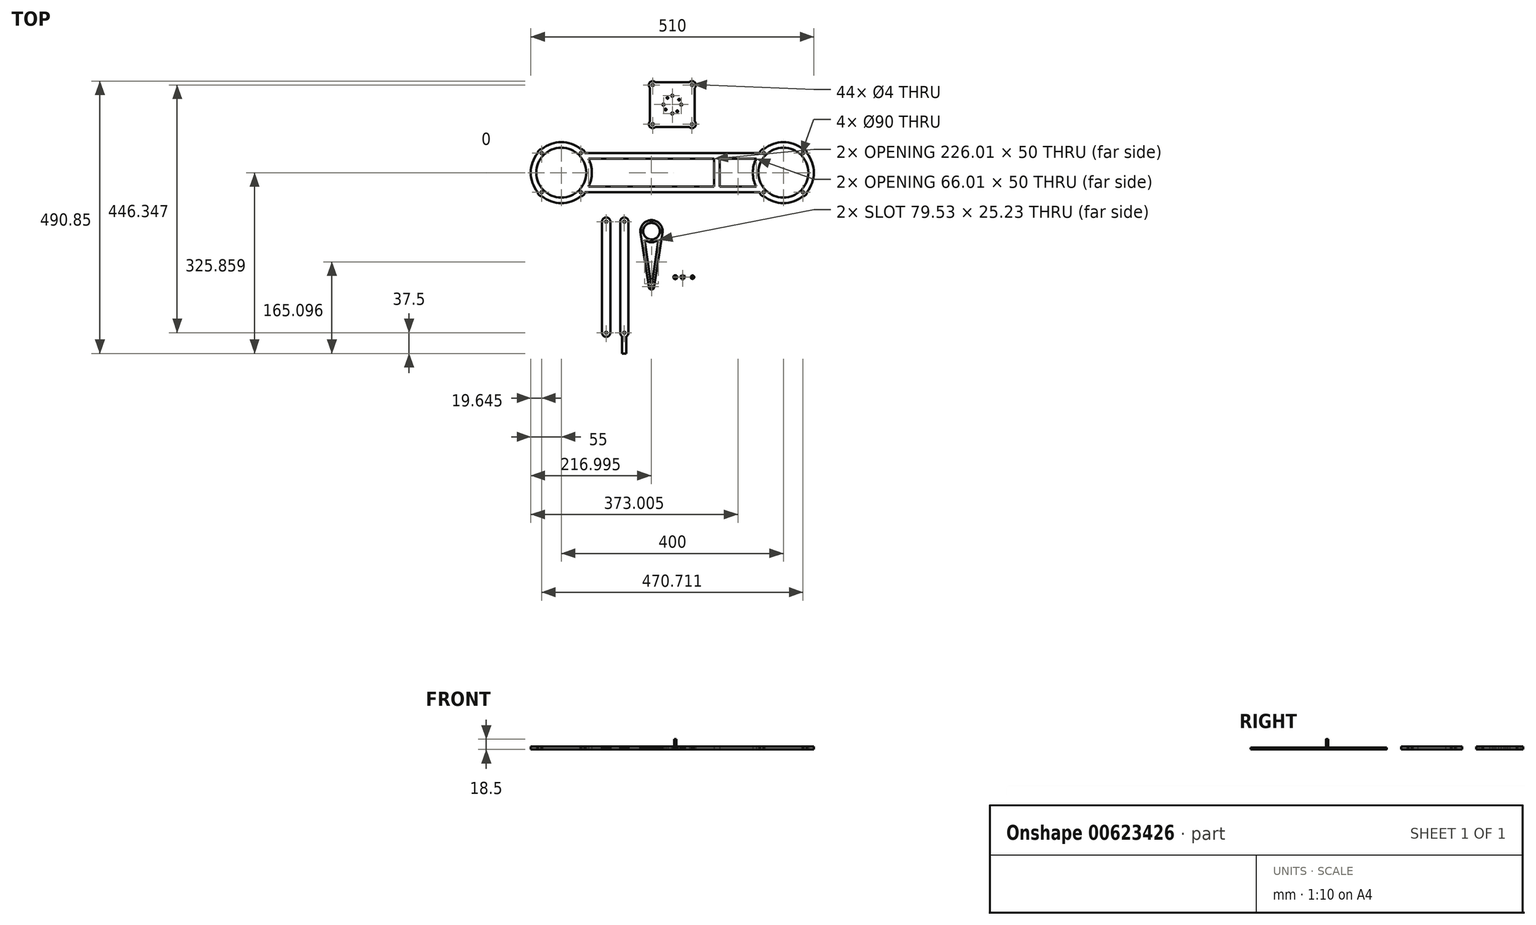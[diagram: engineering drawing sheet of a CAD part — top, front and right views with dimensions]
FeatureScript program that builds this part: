
annotation { "Feature Type Name" : "Feature", "Feature Type Description" : "" }
export const myFeature = defineFeature(function(context is Context, id is Id, definition is map)
    precondition{}
    {
        {
            assignVariable(context, id + "F0", {"name" : "AluThickness", "anyValue" : 3});
        }
        {
            var Q0;
            Q0=qCreatedBy(makeId("Top.planeOp"),FACE);
            var sketch = newSketch(context, id + "F1", { "sketchPlane" : qUnion([Q0])});
            skLineSegment(sketch, "E0.bottom", {"start": v(-111.65, 100) * mm, "end": v(-126.65, 100) * mm});
            skLineSegment(sketch, "E0.top", {"start": v(-111.65, -100) * mm, "end": v(-126.65, -100) * mm});
            skLineSegment(sketch, "E0.left", {"start": v(-111.65, 100) * mm, "end": v(-111.65, -100) * mm});
            skLineSegment(sketch, "E0.right", {"start": v(-126.65, 100) * mm, "end": v(-126.65, -100) * mm});
            skPoint(sketch, "E0.middle", {"position": v(-119.15, 0) * mm});
            skCircle(sketch, "E1", {"center": v(-119.15, 100) * mm, "radius": 7.5 * mm});
            skCircle(sketch, "E2", {"center": v(-119.15, -100) * mm, "radius": 7.5 * mm});
            skLineSegment(sketch, "E3.bottom", {"start": v(-79.02, 100) * mm, "end": v(-94.02, 100) * mm});
            skLineSegment(sketch, "E3.top", {"start": v(-79.02, -100) * mm, "end": v(-94.02, -100) * mm});
            skLineSegment(sketch, "E3.left", {"start": v(-79.02, 100) * mm, "end": v(-79.02, -100) * mm});
            skLineSegment(sketch, "E3.right", {"start": v(-94.02, 100) * mm, "end": v(-94.02, -100) * mm});
            skPoint(sketch, "E3.middle", {"position": v(-86.52, 0) * mm});
            skCircle(sketch, "E4", {"center": v(-86.52, 100) * mm, "radius": 7.5 * mm});
            skCircle(sketch, "E5", {"center": v(-86.52, -100) * mm, "radius": 7.5 * mm});
            skCircle(sketch, "E6", {"center": v(-119.15, 100) * mm, "radius": 2 * mm});
            skCircle(sketch, "E7", {"center": v(-119.15, -100) * mm, "radius": 2 * mm});
            skCircle(sketch, "E8", {"center": v(-86.52, 100) * mm, "radius": 2 * mm});
            skCircle(sketch, "E9", {"center": v(-86.52, -100) * mm, "radius": 2 * mm});
            skLineSegment(sketch, "E10.bottom", {"start": v(-82.93, -137.5) * mm, "end": v(-90.43, -137.5) * mm});
            skLineSegment(sketch, "E10.left", {"start": v(-82.93, -137.5) * mm, "end": v(-82.93, -106.59) * mm});
            skLineSegment(sketch, "E10.right", {"start": v(-90.43, -137.5) * mm, "end": v(-90.43, -106.4) * mm});
            skPoint(sketch, "E10.middle", {"position": v(-86.68, -107.5) * mm});
            skPoint(sketch, "E10.top.end.orphan", {"position": v(-90.43, -77.5) * mm});
            skPoint(sketch, "E11.orphan", {"position": v(-82.93, -77.5) * mm});
            skCircle(sketch, "E12", {"center": v(-37.56, 82.88) * mm, "radius": 20 * mm});
            skCircle(sketch, "E13", {"center": v(-37.56, -17.12) * mm, "radius": 2 * mm});
            skCircle(sketch, "E14.0", {"center": v(-37.56, -17.12) * mm, "radius": 5 * mm});
            skLineSegment(sketch, "E15", {"start": v(-57.56, 82.88) * mm, "end": v(-42.56, -17.12) * mm});
            skLineSegment(sketch, "E16", {"start": v(-32.56, -17.12) * mm, "end": v(-17.56, 82.88) * mm});
            skCircle(sketch, "E17", {"center": v(-37.56, 82.88) * mm, "radius": 15 * mm});
            skCircle(sketch, "E18", {"center": v(-37.56, 82.88) * mm, "radius": 17.5 * mm, "construction": true});
            skCircle(sketch, "E19", {"center": v(-37.56, 100.38) * mm, "radius": 1.5 * mm});
            skCircle(sketch, "E20.1.0", {"center": v(-55.06, 82.88) * mm, "radius": 1.5 * mm});
            skCircle(sketch, "E20.2.0", {"center": v(-37.56, 65.38) * mm, "radius": 1.5 * mm});
            skCircle(sketch, "E20.3.0", {"center": v(-20.06, 82.88) * mm, "radius": 1.5 * mm});
            skLineSegment(sketch, "E21.0", {"start": v(-52.61, 83.62) * mm, "end": v(-52.55, 83.22) * mm});
            skLineSegment(sketch, "E22.trimOffspring", {"start": v(-50.18, 67.36) * mm, "end": v(-38.25, -12.17) * mm});
            skLineSegment(sketch, "E23.trimOffspring", {"start": v(-22.56, 83.22) * mm, "end": v(-22.5, 83.62) * mm});
            skLineSegment(sketch, "E24.trimOffspring", {"start": v(-36.87, -12.17) * mm, "end": v(-24.94, 67.36) * mm});
            skSolve(sketch);
        }
        {
            var Q0;
            Q0 = qSketchRegion(id + "F1", true);
            extrude(context, id + "F2", {"entities" : qUnion([Q0]), "depth" : (getVariable(context, 'AluThickness')) * mm, "offsetDistance" : 25 * mm});
        }
        {
            var Q0;
            Q0=qCreatedBy(makeId("Top.planeOp"),FACE);
            var sketch = newSketch(context, id + "F3", { "sketchPlane" : qUnion([Q0])});
            skCircle(sketch, "E25", {"center": v(5.28, 0) * mm, "radius": 3.5 * mm});
            skCircle(sketch, "E26.cCircle", {"center": v(18.64, 0) * mm, "radius": 3.5 * mm, "construction": true});
            skLineSegment(sketch, "E26.0", {"start": v(20.66, -3.5) * mm, "end": v(16.62, -3.5) * mm});
            skLineSegment(sketch, "E26.1", {"start": v(16.62, -3.5) * mm, "end": v(14.6, 0) * mm});
            skLineSegment(sketch, "E26.2", {"start": v(14.6, 0) * mm, "end": v(16.62, 3.5) * mm});
            skLineSegment(sketch, "E26.3", {"start": v(16.62, 3.5) * mm, "end": v(20.66, 3.5) * mm});
            skLineSegment(sketch, "E26.4", {"start": v(20.66, 3.5) * mm, "end": v(22.68, 0) * mm});
            skLineSegment(sketch, "E26.5", {"start": v(22.68, 0) * mm, "end": v(20.66, -3.5) * mm});
            skPoint(sketch, "E26.0.midPoint", {"position": v(18.64, -3.5) * mm});
            skCircle(sketch, "E27", {"center": v(18.64, 0) * mm, "radius": 2 * mm});
            skCircle(sketch, "E28", {"center": v(36.28, 0) * mm, "radius": 3 * mm});
            skCircle(sketch, "E29", {"center": v(36.28, 0) * mm, "radius": 2 * mm});
            skSolve(sketch);
        }
        {
            var Q0;
            Q0=makeQuery(id+"F3.imprint","IMPRINT",FACE,{"disambiguationData":[TD([[makeQuery(id+"F3.imprint","IMPRINT",EDGE,{"derivedFrom":sQuery(id+"F3.wireOp",EDGE,"E25")}),1.0]])]});
            var Q1;
            Q1=makeQuery(id+"F3.imprint","IMPRINT",FACE,{"disambiguationData":[TD([[makeQuery(id+"F3.imprint","IMPRINT",EDGE,{"derivedFrom":sQuery(id+"F3.wireOp",EDGE,"E26.0")}),-1.0]])]});
            extrude(context, id + "F4", {"entities" : qUnion([Q0, Q1]), "depth" : 3 * mm, "offsetDistance" : 25 * mm});
        }
        {
            var Q0;
            Q0=makeQuery(id+"F3.imprint","IMPRINT",FACE,{"disambiguationData":[TD([[makeQuery(id+"F3.imprint","IMPRINT",EDGE,{"derivedFrom":sQuery(id+"F3.wireOp",EDGE,"E28")}),1.0]])]});
            extrude(context, id + "F5", {"entities" : qUnion([Q0]), "depth" : 1 * mm, "offsetDistance" : 25 * mm});
        }
        {
            var Q0;
            Q0=makeQuery(id+"F5.opExtrude","CAP_FACE",FACE,{"disambiguationData":[OSD([sQuery(id+"F3.wireOp",EDGE,"E28"),sQuery(id+"F3.wireOp",EDGE,"E29")])],"isStart":false});
            var sketch = newSketch(context, id + "F6", { "sketchPlane" : qUnion([Q0])});
            skCircle(sketch, "E30", {"center": v(36.28, 0) * mm, "radius": 3.1 * mm});
            skSolve(sketch);
        }
        {
            var Q0;
            Q0=makeQuery(id+"F3.imprint","IMPRINT",FACE,{"disambiguationData":[TD([[makeQuery(id+"F3.imprint","IMPRINT",EDGE,{"derivedFrom":sQuery(id+"F3.wireOp",EDGE,"E29")}),1.0]])]});
            var sketch = newSketch(context, id + "F7", { "sketchPlane" : qUnion([Q0])});
            skCircle(sketch, "E31", {"center": v(36.28, 0) * mm, "radius": 3.1 * mm});
            skSolve(sketch);
        }
        {
            var Q0;
            Q0=makeQuery(id+"F6.imprint","IMPRINT",FACE,{"disambiguationData":[TD([[makeQuery(id+"F6.imprint","IMPRINT",EDGE,{"derivedFrom":sQuery(id+"F6.wireOp",EDGE,"E30")}),1.0]])]});
            var Q1;
            Q1=makeQuery(id+"F6.imprint","IMPRINT",FACE,{"disambiguationData":[TD([[makeQuery(id+"F6.imprint","IMPRINT",EDGE,{"derivedFrom":makeQuery(id+"F5.opExtrude","CAP_EDGE",EDGE,{"disambiguationData":[OSD([sQuery(id+"F3.wireOp",EDGE,"E28")])],"isStart":false})}),1.0]])]});
            extrude(context, id + "F8", {"entities" : qUnion([Q0, Q1]), "operationType" : NewBodyOperationType.ADD, "depth" : .5 * mm, "offsetDistance" : 25 * mm});
        }
        {
            var Q0;
            Q0=makeQuery(id+"F7.imprint","IMPRINT",FACE,{"disambiguationData":[TD([[makeQuery(id+"F7.imprint","IMPRINT",EDGE,{"derivedFrom":sQuery(id+"F7.wireOp",EDGE,"E31")}),1.0]])]});
            extrude(context, id + "F9", {"entities" : qUnion([Q0]), "operationType" : NewBodyOperationType.ADD, "oppositeDirection" : true, "depth" : .5 * mm, "offsetDistance" : 25 * mm});
        }
        {
            var Q0;
            Q0=makeQuery(id+"F4.opExtrude","CAP_FACE",FACE,{"disambiguationData":[OSD([sQuery(id+"F3.wireOp",EDGE,"E25")])],"isStart":true});
            var sketch = newSketch(context, id + "F10", { "sketchPlane" : qUnion([Q0])});
            skCircle(sketch, "E32.cCircle", {"center": v(5.28, 0) * mm, "radius": 2 * mm, "construction": true});
            skLineSegment(sketch, "E32.0", {"start": v(6.44, -2) * mm, "end": v(4.13, -2) * mm});
            skLineSegment(sketch, "E32.1", {"start": v(4.13, -2) * mm, "end": v(2.97, 0) * mm});
            skLineSegment(sketch, "E32.2", {"start": v(2.97, 0) * mm, "end": v(4.13, 2) * mm});
            skLineSegment(sketch, "E32.3", {"start": v(4.13, 2) * mm, "end": v(6.44, 2) * mm});
            skLineSegment(sketch, "E32.4", {"start": v(6.44, 2) * mm, "end": v(7.59, 0) * mm});
            skLineSegment(sketch, "E32.5", {"start": v(7.59, 0) * mm, "end": v(6.44, -2) * mm});
            skPoint(sketch, "E32.0.midPoint", {"position": v(5.28, -2) * mm});
            skSolve(sketch);
        }
        {
            var Q0;
            Q0=makeQuery(id+"F10.imprint","IMPRINT",FACE,{"disambiguationData":[TD([[makeQuery(id+"F10.imprint","IMPRINT",EDGE,{"derivedFrom":sQuery(id+"F10.wireOp",EDGE,"E32.0")}),-1.0]])]});
            extrude(context, id + "F11", {"entities" : qUnion([Q0]), "operationType" : NewBodyOperationType.REMOVE, "oppositeDirection" : true, "depth" : 2 * mm, "offsetDistance" : 25 * mm});
        }
        {
            var Q0;
            Q0=makeQuery(id+"F4.opExtrude","CAP_FACE",FACE,{"disambiguationData":[OSD([sQuery(id+"F3.wireOp",EDGE,"E25")])],"isStart":false});
            var sketch = newSketch(context, id + "F12", { "sketchPlane" : qUnion([Q0])});
            skCircle(sketch, "E33", {"center": v(5.28, 0) * mm, "radius": 2 * mm});
            skSolve(sketch);
        }
        {
            var Q0;
            Q0=makeQuery(id+"F12.imprint","IMPRINT",FACE,{"disambiguationData":[TD([[makeQuery(id+"F12.imprint","IMPRINT",EDGE,{"derivedFrom":sQuery(id+"F12.wireOp",EDGE,"E33")}),1.0]])]});
            extrude(context, id + "F13", {"entities" : qUnion([Q0]), "operationType" : NewBodyOperationType.ADD, "depth" : (getVariable(context, 'AluThickness') * 5) * mm, "offsetDistance" : 25 * mm});
        }
        {
            var Q0;
            Q0=qCreatedBy(makeId("Top.planeOp"),FACE);
            var sketch = newSketch(context, id + "F14", { "sketchPlane" : qUnion([Q0])});
            skLineSegment(sketch, "E34.bottom", {"start": v(151.01, 163.36) * mm, "end": v(-162.58, 163.36) * mm});
            skLineSegment(sketch, "E34.top", {"start": v(151.01, 213.36) * mm, "end": v(-162.58, 213.36) * mm});
            skPoint(sketch, "E34.middle", {"position": v(0, 188.36) * mm});
            skCircle(sketch, "E35", {"center": v(-200, 188.36) * mm, "radius": 45 * mm});
            skCircle(sketch, "E36.MirrorC", {"center": v(200, 188.36) * mm, "radius": 45 * mm});
            skCircle(sketch, "E37.0", {"center": v(-200, 188.36) * mm, "radius": 55 * mm});
            skLineSegment(sketch, "E38.0", {"start": v(157.57, 153.36) * mm, "end": v(-157.57, 153.36) * mm});
            skCircle(sketch, "E39.0", {"center": v(200, 188.36) * mm, "radius": 55 * mm});
            skPoint(sketch, "E40.orphan", {"position": v(-200, 163.36) * mm});
            skPoint(sketch, "E34.right.end.orphan", {"position": v(-200, 213.36) * mm});
            skLineSegment(sketch, "E41.trimOffspring", {"start": v(157.57, 223.36) * mm, "end": v(-157.57, 223.36) * mm});
            skPoint(sketch, "E42.orphan", {"position": v(200, 163.36) * mm});
            skPoint(sketch, "E43.orphan", {"position": v(200, 213.36) * mm});
            skCircle(sketch, "E44.0", {"center": v(-200, 188.36) * mm, "radius": 50 * mm, "construction": true});
            skLineSegment(sketch, "E45.bottom", {"start": v(-235.36, 223.71) * mm, "end": v(-164.64, 223.71) * mm, "construction": true});
            skLineSegment(sketch, "E45.top", {"start": v(-235.36, 153) * mm, "end": v(-164.64, 153) * mm, "construction": true});
            skLineSegment(sketch, "E45.left", {"start": v(-235.36, 223.71) * mm, "end": v(-235.36, 153) * mm, "construction": true});
            skLineSegment(sketch, "E45.right", {"start": v(-164.64, 223.71) * mm, "end": v(-164.64, 153) * mm, "construction": true});
            skCircle(sketch, "E46", {"center": v(-235.36, 223.71) * mm, "radius": 2 * mm});
            skCircle(sketch, "E47.0", {"center": v(-235.36, 223.71) * mm, "radius": 7 * mm});
            skCircle(sketch, "E48.1.0", {"center": v(-235.36, 153) * mm, "radius": 2 * mm});
            skCircle(sketch, "E48.1.1", {"center": v(-235.36, 153) * mm, "radius": 7 * mm});
            skCircle(sketch, "E48.2.0", {"center": v(-164.64, 153) * mm, "radius": 2 * mm});
            skCircle(sketch, "E48.2.1", {"center": v(-164.64, 153) * mm, "radius": 7 * mm});
            skCircle(sketch, "E48.3.0", {"center": v(-164.64, 223.71) * mm, "radius": 2 * mm});
            skCircle(sketch, "E48.3.1", {"center": v(-164.64, 223.71) * mm, "radius": 7 * mm});
            skCircle(sketch, "E49.MirrorC", {"center": v(235.36, 223.71) * mm, "radius": 2 * mm});
            skCircle(sketch, "E50.MirrorC", {"center": v(235.36, 223.71) * mm, "radius": 7 * mm});
            skCircle(sketch, "E51.MirrorC", {"center": v(164.64, 223.71) * mm, "radius": 7 * mm});
            skCircle(sketch, "E52.MirrorC", {"center": v(164.64, 153) * mm, "radius": 7 * mm});
            skCircle(sketch, "E53.MirrorC", {"center": v(164.64, 153) * mm, "radius": 2 * mm});
            skCircle(sketch, "E54.MirrorC", {"center": v(235.36, 153) * mm, "radius": 7 * mm});
            skCircle(sketch, "E55.MirrorC", {"center": v(235.36, 153) * mm, "radius": 2 * mm});
            skCircle(sketch, "E56", {"center": v(164.64, 223.71) * mm, "radius": 2 * mm});
            skLineSegment(sketch, "E57", {"start": v(0, 213.36) * mm, "end": v(0, 163.36) * mm, "construction": true});
            skPoint(sketch, "E57.endSnap0", {"position": v(0, 153.36) * mm});
            skLineSegment(sketch, "E58", {"start": v(-80, 213.36) * mm, "end": v(-80, 163.36) * mm, "construction": true});
            skLineSegment(sketch, "E59.MirrorCS", {"start": v(80, 213.36) * mm, "end": v(80, 163.36) * mm, "construction": true});
            skLineSegment(sketch, "E60.bottom", {"start": v(-75, 163.36) * mm, "end": v(-85, 163.36) * mm});
            skLineSegment(sketch, "E60.top", {"start": v(-75, 213.36) * mm, "end": v(-85, 213.36) * mm});
            skLineSegment(sketch, "E60.left", {"start": v(-75, 163.36) * mm, "end": v(-75, 213.36) * mm});
            skLineSegment(sketch, "E60.right", {"start": v(-85, 163.36) * mm, "end": v(-85, 213.36) * mm});
            skPoint(sketch, "E60.middle", {"position": v(-80, 188.36) * mm});
            skLineSegment(sketch, "E61.MirrorCS", {"start": v(85, 163.36) * mm, "end": v(85, 213.36) * mm});
            skLineSegment(sketch, "E62.MirrorCS", {"start": v(75, 163.36) * mm, "end": v(75, 213.36) * mm});
            skSolve(sketch);
        }
        {
            var Q0;
            Q0 = qSketchRegion(id + "F14", true);
            var Q1;
            {var subQ0=sQuery(id+"F14.wireOp",EDGE,"E35");var subQ1=sQuery(id+"F14.wireOp",EDGE,"E34.bottom");var subQ2=makeQuery(id+"F14.imprint","INTERSECT",VERTEX,{"derivedFrom":[subQ1,subQ0]});Q1=makeQuery(id+"F14.imprint","IMPRINT",FACE,{"disambiguationData":[TD([[makeQuery(id+"F14.imprint","IMPRINT",EDGE,{"disambiguationData":[TD([[subQ2,1.0]])],"derivedFrom":subQ1}),-1.0]])]});}
            var Q2;
            Q2=makeQuery(id+"F14.imprint","IMPRINT",FACE,{"disambiguationData":[TD([[makeQuery(id+"F14.imprint","IMPRINT",EDGE,{"derivedFrom":sQuery(id+"F14.wireOp",EDGE,"E60.bottom")}),-1.0]])]});
            var Q3;
            {var subQ0=sQuery(id+"F14.wireOp",EDGE,"E61.MirrorCS");Q3=makeQuery(id+"F14.imprint","IMPRINT",FACE,{"disambiguationData":[TD([[makeQuery(id+"F14.imprint","IMPRINT",EDGE,{"derivedFrom":subQ0}),1.0]])]});}
            extrude(context, id + "F15", {"entities" : qUnion([Q0, Q1, Q2, Q3]), "depth" : 5 * mm, "offsetDistance" : 25 * mm});
        }
        {
            var Q0;
            Q0=qCreatedBy(makeId("Top.planeOp"),FACE);
            var sketch = newSketch(context, id + "F16", { "sketchPlane" : qUnion([Q0])});
            skLineSegment(sketch, "E63.bottom", {"start": v(35.35, 275.64) * mm, "end": v(-35.35, 275.64) * mm, "construction": true});
            skLineSegment(sketch, "E63.top", {"start": v(35.36, 346.35) * mm, "end": v(-35.35, 346.35) * mm, "construction": true});
            skLineSegment(sketch, "E63.left", {"start": v(35.35, 275.64) * mm, "end": v(35.35, 346.35) * mm, "construction": true});
            skLineSegment(sketch, "E63.right", {"start": v(-35.35, 275.64) * mm, "end": v(-35.35, 346.35) * mm, "construction": true});
            skPoint(sketch, "E63.middle", {"position": v(0, 311) * mm});
            skCircle(sketch, "E64", {"center": v(-35.35, 346.35) * mm, "radius": 2 * mm});
            skCircle(sketch, "E65.1.0", {"center": v(-35.35, 275.64) * mm, "radius": 2 * mm});
            skCircle(sketch, "E65.2.0", {"center": v(35.35, 275.64) * mm, "radius": 2 * mm});
            skCircle(sketch, "E65.3.0", {"center": v(35.35, 346.35) * mm, "radius": 2 * mm});
            skArc(sketch, "E66.0", {"start": v(-30.46, 351.35) * mm, "mid": v(-40.3, 351.3) * mm, "end": v(-40.36, 341.45) * mm});
            skLineSegment(sketch, "E67.0", {"start": v(30.46, 351.35) * mm, "end": v(-30.46, 351.35) * mm});
            skArc(sketch, "E68.0", {"start": v(40.35, 341.45) * mm, "mid": v(40.3, 351.3) * mm, "end": v(30.46, 351.35) * mm});
            skLineSegment(sketch, "E69.0", {"start": v(40.35, 280.54) * mm, "end": v(40.35, 341.45) * mm});
            skArc(sketch, "E70.0", {"start": v(30.46, 270.64) * mm, "mid": v(40.3, 270.69) * mm, "end": v(40.35, 280.54) * mm});
            skLineSegment(sketch, "E71.0", {"start": v(30.46, 270.64) * mm, "end": v(-30.46, 270.64) * mm});
            skLineSegment(sketch, "E72.0", {"start": v(-40.36, 280.54) * mm, "end": v(-40.36, 346.35) * mm});
            skArc(sketch, "E73.0", {"start": v(-40.36, 280.54) * mm, "mid": v(-40.3, 270.69) * mm, "end": v(-30.46, 270.64) * mm});
            skCircle(sketch, "E74", {"center": v(0, 311) * mm, "radius": 16 * mm, "construction": true});
            skCircle(sketch, "E75", {"center": v(0, 327) * mm, "radius": 2 * mm});
            skCircle(sketch, "E76.1.0", {"center": v(-16, 311) * mm, "radius": 2 * mm});
            skCircle(sketch, "E76.2.0", {"center": v(0, 295) * mm, "radius": 2 * mm});
            skCircle(sketch, "E76.3.0", {"center": v(16, 311) * mm, "radius": 2 * mm});
            skCircle(sketch, "E77", {"center": v(0, 311) * mm, "radius": 15 * mm, "construction": true});
            skCircle(sketch, "E78", {"center": v(12.13, 319.82) * mm, "radius": 1.5 * mm});
            skCircle(sketch, "E79.1.0", {"center": v(-8.83, 323.12) * mm, "radius": 1.5 * mm});
            skCircle(sketch, "E79.2.0", {"center": v(-12.13, 302.16) * mm, "radius": 1.5 * mm});
            skCircle(sketch, "E79.3.0", {"center": v(8.83, 298.87) * mm, "radius": 1.5 * mm});
            skSolve(sketch);
        }
        {
            var Q0;
            Q0=makeQuery(id+"F16.imprint","IMPRINT",FACE,{"disambiguationData":[TD([[makeQuery(id+"F16.imprint","IMPRINT",EDGE,{"derivedFrom":sQuery(id+"F16.wireOp",EDGE,"E64")}),-1.0]])]});
            extrude(context, id + "F17", {"entities" : qUnion([Q0]), "depth" : 5 * mm, "offsetDistance" : 25 * mm});
        }
    });
